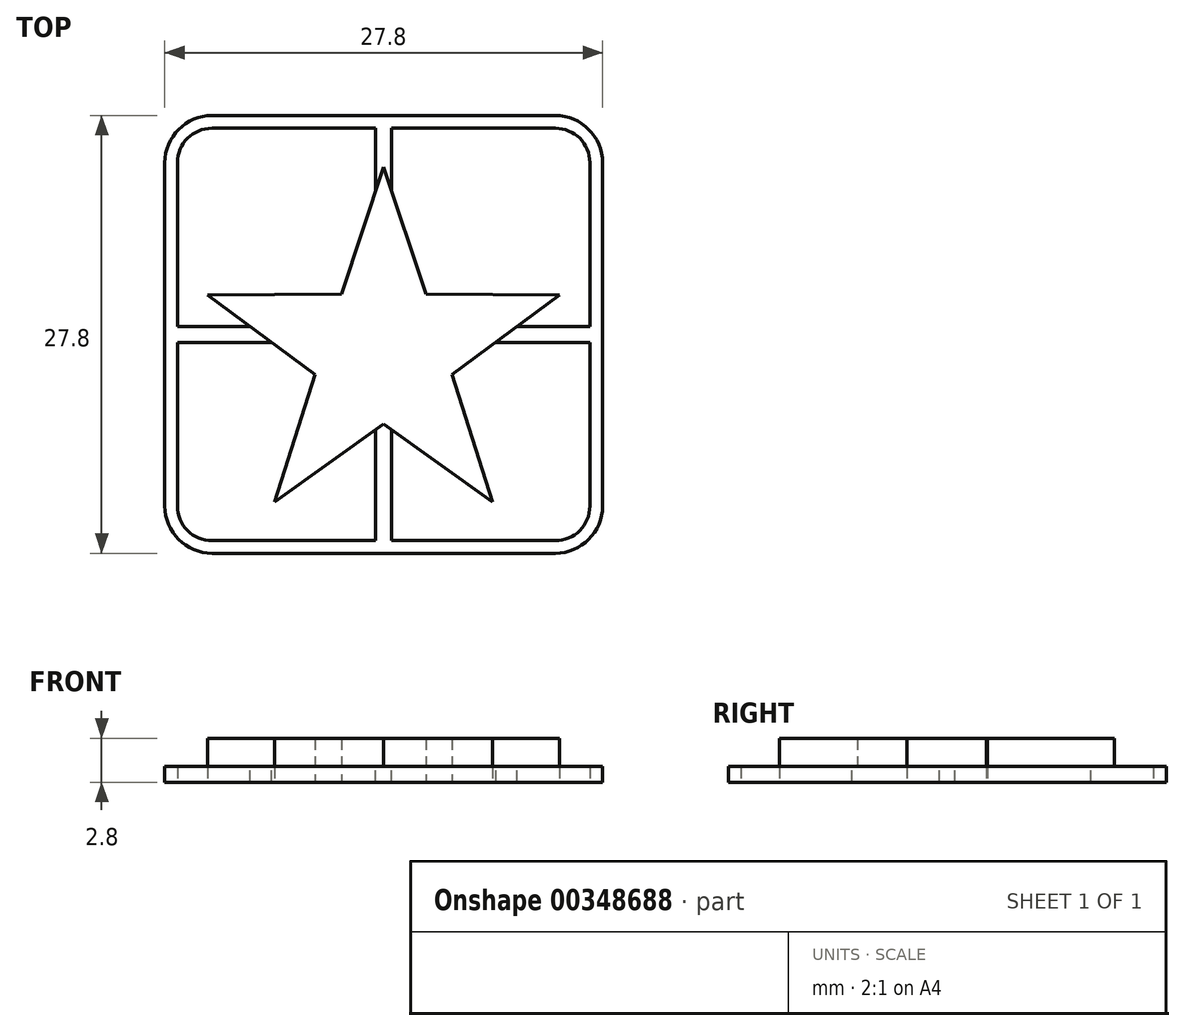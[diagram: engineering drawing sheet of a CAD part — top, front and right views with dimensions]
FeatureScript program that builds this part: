
annotation { "Feature Type Name" : "Feature", "Feature Type Description" : "" }
export const myFeature = defineFeature(function(context is Context, id is Id, definition is map)
    precondition{}
    {
        {
            var Q0;
            Q0=qCreatedBy(makeId("Top.planeOp"),FACE);
            var sketch = newSketch(context, id + "F0", { "sketchPlane" : qUnion([Q0])});
            skLineSegment(sketch, "E0", {"start": v(-13.9, 10.9) * mm, "end": v(-13.9, -10.9) * mm});
            skLineSegment(sketch, "E1", {"start": v(13.9, -10.9) * mm, "end": v(13.9, 10.9) * mm});
            skLineSegment(sketch, "E2", {"start": v(-10.9, 13.9) * mm, "end": v(10.9, 13.9) * mm});
            skLineSegment(sketch, "E3", {"start": v(-10.9, -13.9) * mm, "end": v(10.9, -13.9) * mm});
            skLineSegment(sketch, "E4", {"start": v(0, 13.9) * mm, "end": v(0, -13.9) * mm, "construction": true});
            skLineSegment(sketch, "E5", {"start": v(-13.9, 0) * mm, "end": v(13.9, 0) * mm, "construction": true});
            skPoint(sketch, "E6", {"position": v(0, 0) * mm});
            skPoint(sketch, "E7", {"position": v(0, 13.9) * mm});
            skPoint(sketch, "E8", {"position": v(0, -13.9) * mm});
            skPoint(sketch, "E9", {"position": v(-13.9, 0) * mm});
            skPoint(sketch, "E10", {"position": v(13.9, 0) * mm});
            skArc(sketch, "E11", {"start": v(-10.9, 13.9) * mm, "mid": v(-13.02, 13.02) * mm, "end": v(-13.9, 10.9) * mm});
            skArc(sketch, "E12", {"start": v(13.9, 10.9) * mm, "mid": v(13.02, 13.02) * mm, "end": v(10.9, 13.9) * mm});
            skArc(sketch, "E13", {"start": v(-13.9, -10.9) * mm, "mid": v(-13.02, -13.02) * mm, "end": v(-10.9, -13.9) * mm});
            skArc(sketch, "E14", {"start": v(10.9, -13.9) * mm, "mid": v(13.02, -13.02) * mm, "end": v(13.9, -10.9) * mm});
            skLineSegment(sketch, "E15", {"start": v(-0.5, 13.1) * mm, "end": v(-0.5, 0.5) * mm});
            skLineSegment(sketch, "E16", {"start": v(-0.5, 0.5) * mm, "end": v(-13.1, 0.5) * mm});
            skLineSegment(sketch, "E17", {"start": v(-13.1, 0.5) * mm, "end": v(-13.1, 10.9) * mm});
            skLineSegment(sketch, "E18", {"start": v(-0.5, 13.1) * mm, "end": v(-10.9, 13.1) * mm});
            skArc(sketch, "E19", {"start": v(-10.9, 13.1) * mm, "mid": v(-12.46, 12.46) * mm, "end": v(-13.1, 10.9) * mm});
            skLineSegment(sketch, "E20.MirrorCS", {"start": v(13.1, 0.5) * mm, "end": v(13.1, 10.9) * mm});
            skLineSegment(sketch, "E21.MirrorCS", {"start": v(0.5, 0.5) * mm, "end": v(13.1, 0.5) * mm});
            skLineSegment(sketch, "E22.MirrorCS", {"start": v(0.5, 13.1) * mm, "end": v(10.9, 13.1) * mm});
            skLineSegment(sketch, "E23.MirrorCS", {"start": v(0.5, 13.1) * mm, "end": v(0.5, 0.5) * mm});
            skArc(sketch, "E24.MirrorCS", {"start": v(10.9, 13.1) * mm, "mid": v(12.46, 12.46) * mm, "end": v(13.1, 10.9) * mm});
            skLineSegment(sketch, "E25.MirrorCS", {"start": v(0.5, -13.1) * mm, "end": v(10.9, -13.1) * mm});
            skLineSegment(sketch, "E26.MirrorCS", {"start": v(13.1, -0.5) * mm, "end": v(13.1, -10.9) * mm});
            skArc(sketch, "E27.MirrorCS", {"start": v(10.9, -13.1) * mm, "mid": v(12.46, -12.46) * mm, "end": v(13.1, -10.9) * mm});
            skLineSegment(sketch, "E28.MirrorCS", {"start": v(0.5, -13.1) * mm, "end": v(0.5, -0.5) * mm});
            skLineSegment(sketch, "E29.MirrorCS", {"start": v(0.5, -0.5) * mm, "end": v(13.1, -0.5) * mm});
            skLineSegment(sketch, "E30.MirrorCS", {"start": v(-0.5, -0.5) * mm, "end": v(-13.1, -0.5) * mm});
            skLineSegment(sketch, "E31.MirrorCS", {"start": v(-0.5, -13.1) * mm, "end": v(-0.5, -0.5) * mm});
            skLineSegment(sketch, "E32.MirrorCS", {"start": v(-0.5, -13.1) * mm, "end": v(-10.9, -13.1) * mm});
            skLineSegment(sketch, "E33.MirrorCS", {"start": v(-13.1, -0.5) * mm, "end": v(-13.1, -10.9) * mm});
            skArc(sketch, "E34.MirrorCS", {"start": v(-10.9, -13.1) * mm, "mid": v(-12.46, -12.46) * mm, "end": v(-13.1, -10.9) * mm});
            skSolve(sketch);
        }
        {
            var Q0;
            Q0=makeQuery(id+"F0.imprint","IMPRINT",FACE,{"disambiguationData":[TD([[makeQuery(id+"F0.imprint","IMPRINT",EDGE,{"derivedFrom":sQuery(id+"F0.wireOp",EDGE,"E0")}),1.0]])]});
            extrude(context, id + "F1", {"entities" : qUnion([Q0]), "depth" : 1 * mm});
        }
        {
            var Q0;
            Q0=makeQuery(id+"F1.opExtrude","CAP_FACE",FACE,{"disambiguationData":[OSD([sQuery(id+"F0.wireOp",EDGE,"E0"),sQuery(id+"F0.wireOp",EDGE,"E1"),sQuery(id+"F0.wireOp",EDGE,"E2"),sQuery(id+"F0.wireOp",EDGE,"E3"),sQuery(id+"F0.wireOp",EDGE,"E11"),sQuery(id+"F0.wireOp",EDGE,"E12"),sQuery(id+"F0.wireOp",EDGE,"E13"),sQuery(id+"F0.wireOp",EDGE,"E14"),sQuery(id+"F0.wireOp",EDGE,"E15"),sQuery(id+"F0.wireOp",EDGE,"E16"),sQuery(id+"F0.wireOp",EDGE,"E17"),sQuery(id+"F0.wireOp",EDGE,"E18"),sQuery(id+"F0.wireOp",EDGE,"E19"),sQuery(id+"F0.wireOp",EDGE,"E20.MirrorCS"),sQuery(id+"F0.wireOp",EDGE,"E21.MirrorCS"),sQuery(id+"F0.wireOp",EDGE,"E22.MirrorCS"),sQuery(id+"F0.wireOp",EDGE,"E23.MirrorCS"),sQuery(id+"F0.wireOp",EDGE,"E24.MirrorCS"),sQuery(id+"F0.wireOp",EDGE,"E25.MirrorCS"),sQuery(id+"F0.wireOp",EDGE,"E26.MirrorCS"),sQuery(id+"F0.wireOp",EDGE,"E27.MirrorCS"),sQuery(id+"F0.wireOp",EDGE,"E28.MirrorCS"),sQuery(id+"F0.wireOp",EDGE,"E29.MirrorCS"),sQuery(id+"F0.wireOp",EDGE,"E30.MirrorCS"),sQuery(id+"F0.wireOp",EDGE,"E31.MirrorCS"),sQuery(id+"F0.wireOp",EDGE,"E32.MirrorCS"),sQuery(id+"F0.wireOp",EDGE,"E33.MirrorCS"),sQuery(id+"F0.wireOp",EDGE,"E34.MirrorCS")])],"isStart":false});
            var sketch = newSketch(context, id + "F2", { "sketchPlane" : qUnion([Q0])});
            skCircle(sketch, "E35.cCircle", {"center": v(0, -1.14) * mm, "radius": 9.51 * mm, "construction": true});
            skLineSegment(sketch, "E35.0", {"start": v(6.91, -10.65) * mm, "end": v(-6.91, -10.65) * mm, "construction": true});
            skLineSegment(sketch, "E35.1", {"start": v(-6.91, -10.65) * mm, "end": v(-11.18, 2.5) * mm, "construction": true});
            skLineSegment(sketch, "E35.2", {"start": v(-11.18, 2.5) * mm, "end": v(0, 10.62) * mm, "construction": true});
            skLineSegment(sketch, "E35.3", {"start": v(0, 10.62) * mm, "end": v(11.18, 2.5) * mm, "construction": true});
            skLineSegment(sketch, "E35.4", {"start": v(11.18, 2.5) * mm, "end": v(6.91, -10.65) * mm, "construction": true});
            skPoint(sketch, "E35.0.midPoint", {"position": v(0, -10.65) * mm});
            skCircle(sketch, "E36.cCircle", {"center": v(0, -1.14) * mm, "radius": 3.7 * mm, "construction": true});
            skLineSegment(sketch, "E36.0", {"start": v(-2.68, 2.55) * mm, "end": v(2.68, 2.55) * mm, "construction": true});
            skLineSegment(sketch, "E36.1", {"start": v(2.68, 2.55) * mm, "end": v(4.34, -2.55) * mm, "construction": true});
            skLineSegment(sketch, "E36.2", {"start": v(4.34, -2.55) * mm, "end": v(0, -5.7) * mm, "construction": true});
            skLineSegment(sketch, "E36.3", {"start": v(0, -5.7) * mm, "end": v(-4.34, -2.55) * mm, "construction": true});
            skLineSegment(sketch, "E36.4", {"start": v(-4.34, -2.55) * mm, "end": v(-2.68, 2.55) * mm, "construction": true});
            skPoint(sketch, "E36.0.midPoint", {"position": v(0, 2.55) * mm});
            skLineSegment(sketch, "E37", {"start": v(-11.18, 2.5) * mm, "end": v(-2.68, 2.55) * mm});
            skLineSegment(sketch, "E38", {"start": v(-2.68, 2.55) * mm, "end": v(0, 10.62) * mm});
            skLineSegment(sketch, "E39", {"start": v(0, 10.62) * mm, "end": v(2.68, 2.55) * mm});
            skLineSegment(sketch, "E40", {"start": v(2.68, 2.55) * mm, "end": v(11.18, 2.5) * mm});
            skLineSegment(sketch, "E41", {"start": v(11.18, 2.5) * mm, "end": v(4.34, -2.55) * mm});
            skLineSegment(sketch, "E42", {"start": v(4.34, -2.55) * mm, "end": v(6.91, -10.65) * mm});
            skLineSegment(sketch, "E43", {"start": v(6.91, -10.65) * mm, "end": v(0, -5.7) * mm});
            skLineSegment(sketch, "E44", {"start": v(0, -5.7) * mm, "end": v(-6.91, -10.65) * mm});
            skLineSegment(sketch, "E45", {"start": v(-4.34, -2.55) * mm, "end": v(-6.91, -10.65) * mm});
            skLineSegment(sketch, "E46", {"start": v(-4.34, -2.55) * mm, "end": v(-11.18, 2.5) * mm});
            skSolve(sketch);
        }
        {
            var Q0;
            {var subQ6=sQuery(id+"F2.wireOp",EDGE,"E37");Q0=makeQuery(id+"F2.imprint","IMPRINT",FACE,{"disambiguationData":[TD([[makeQuery(id+"F2.imprint","IMPRINT",EDGE,{"derivedFrom":subQ6}),-1.0]])]});}
            var Q1;
            {var subQ8=sQuery(id+"F2.wireOp",EDGE,"E38");var subQ19=sQuery(id+"F2.wireOp",EDGE,"E39");var subQ20=makeQuery(id+"F2.imprint","INTERSECT",VERTEX,{"derivedFrom":[subQ8,subQ19]});Q1=makeQuery(id+"F2.imprint","IMPRINT",FACE,{"disambiguationData":[TD([[makeQuery(id+"F2.imprint","IMPRINT",EDGE,{"disambiguationData":[TD([[subQ20,1.0]])],"derivedFrom":subQ8}),-1.0]])]});}
            var Q2;
            {var subQ5=sQuery(id+"F2.wireOp",EDGE,"E40");Q2=makeQuery(id+"F2.imprint","IMPRINT",FACE,{"disambiguationData":[TD([[makeQuery(id+"F2.imprint","IMPRINT",EDGE,{"derivedFrom":subQ5}),-1.0]])]});}
            var Q3;
            {var subQ5=sQuery(id+"F2.wireOp",EDGE,"E42");Q3=makeQuery(id+"F2.imprint","IMPRINT",FACE,{"disambiguationData":[TD([[makeQuery(id+"F2.imprint","IMPRINT",EDGE,{"derivedFrom":subQ5}),-1.0]])]});}
            var Q4;
            {var subQ5=sQuery(id+"F2.wireOp",EDGE,"E45");Q4=makeQuery(id+"F2.imprint","IMPRINT",FACE,{"disambiguationData":[TD([[makeQuery(id+"F2.imprint","IMPRINT",EDGE,{"derivedFrom":subQ5}),1.0]])]});}
            extrude(context, id + "F3", {"entities" : qUnion([Q0, Q1, Q2, Q3, Q4]), "operationType" : NewBodyOperationType.ADD, "depth" : 1.8 * mm});
        }
        {
            var Q0;
            {var subQ0=sQuery(id+"F2.wireOp",EDGE,"E37");var subQ1=sQuery(id+"F2.wireOp",EDGE,"E46");var subQ3=sQuery(id+"F0.wireOp",EDGE,"E15");var subQ4=sQuery(id+"F2.wireOp",EDGE,"E38");Q0=makeQuery(id+"F3.boolean.opBoolean","SPLIT",FACE,{"disambiguationData":[TD([makeQuery(id+"F1.opExtrude","SWEPT_FACE",FACE,{"disambiguationData":[OSD([subQ3])]})])],"derivedFrom":makeQuery(id+"F3.opExtrude","CAP_FACE",FACE,{"disambiguationData":[OSD([subQ0,subQ4,sQuery(id+"F2.wireOp",EDGE,"E39"),sQuery(id+"F2.wireOp",EDGE,"E40"),sQuery(id+"F2.wireOp",EDGE,"E41"),sQuery(id+"F2.wireOp",EDGE,"E42"),sQuery(id+"F2.wireOp",EDGE,"E43"),sQuery(id+"F2.wireOp",EDGE,"E44"),sQuery(id+"F2.wireOp",EDGE,"E45"),subQ1])],"isStart":true})});}
            var Q1;
            {var subQ1=sQuery(id+"F0.wireOp",EDGE,"E30.MirrorCS");var subQ2=sQuery(id+"F2.wireOp",EDGE,"E44");var subQ3=sQuery(id+"F2.wireOp",EDGE,"E45");var subQ4=sQuery(id+"F2.wireOp",EDGE,"E46");Q1=makeQuery(id+"F3.boolean.opBoolean","SPLIT",FACE,{"disambiguationData":[TD([makeQuery(id+"F1.opExtrude","SWEPT_FACE",FACE,{"disambiguationData":[OSD([subQ1])]})])],"derivedFrom":makeQuery(id+"F3.opExtrude","CAP_FACE",FACE,{"disambiguationData":[OSD([sQuery(id+"F2.wireOp",EDGE,"E37"),sQuery(id+"F2.wireOp",EDGE,"E38"),sQuery(id+"F2.wireOp",EDGE,"E39"),sQuery(id+"F2.wireOp",EDGE,"E40"),sQuery(id+"F2.wireOp",EDGE,"E41"),sQuery(id+"F2.wireOp",EDGE,"E42"),sQuery(id+"F2.wireOp",EDGE,"E43"),subQ2,subQ3,subQ4])],"isStart":true})});}
            var Q2;
            {var subQ0=sQuery(id+"F2.wireOp",EDGE,"E41");var subQ2=sQuery(id+"F0.wireOp",EDGE,"E28.MirrorCS");var subQ3=sQuery(id+"F2.wireOp",EDGE,"E42");var subQ4=sQuery(id+"F2.wireOp",EDGE,"E43");Q2=makeQuery(id+"F3.boolean.opBoolean","SPLIT",FACE,{"disambiguationData":[TD([makeQuery(id+"F1.opExtrude","SWEPT_FACE",FACE,{"disambiguationData":[OSD([subQ2])]})])],"derivedFrom":makeQuery(id+"F3.opExtrude","CAP_FACE",FACE,{"disambiguationData":[OSD([sQuery(id+"F2.wireOp",EDGE,"E37"),sQuery(id+"F2.wireOp",EDGE,"E38"),sQuery(id+"F2.wireOp",EDGE,"E39"),sQuery(id+"F2.wireOp",EDGE,"E40"),subQ0,subQ3,subQ4,sQuery(id+"F2.wireOp",EDGE,"E44"),sQuery(id+"F2.wireOp",EDGE,"E45"),sQuery(id+"F2.wireOp",EDGE,"E46")])],"isStart":true})});}
            var Q3;
            {var subQ1=sQuery(id+"F2.wireOp",EDGE,"E41");var subQ2=sQuery(id+"F0.wireOp",EDGE,"E21.MirrorCS");var subQ3=sQuery(id+"F2.wireOp",EDGE,"E39");var subQ4=sQuery(id+"F2.wireOp",EDGE,"E40");Q3=makeQuery(id+"F3.boolean.opBoolean","SPLIT",FACE,{"disambiguationData":[TD([makeQuery(id+"F1.opExtrude","SWEPT_FACE",FACE,{"disambiguationData":[OSD([subQ2])]})])],"derivedFrom":makeQuery(id+"F3.opExtrude","CAP_FACE",FACE,{"disambiguationData":[OSD([sQuery(id+"F2.wireOp",EDGE,"E37"),sQuery(id+"F2.wireOp",EDGE,"E38"),subQ3,subQ4,subQ1,sQuery(id+"F2.wireOp",EDGE,"E42"),sQuery(id+"F2.wireOp",EDGE,"E43"),sQuery(id+"F2.wireOp",EDGE,"E44"),sQuery(id+"F2.wireOp",EDGE,"E45"),sQuery(id+"F2.wireOp",EDGE,"E46")])],"isStart":true})});}
            extrude(context, id + "F4", {"entities" : qUnion([Q0, Q1, Q2, Q3]), "operationType" : NewBodyOperationType.ADD, "depth" : 1 * mm});
        }
    });
